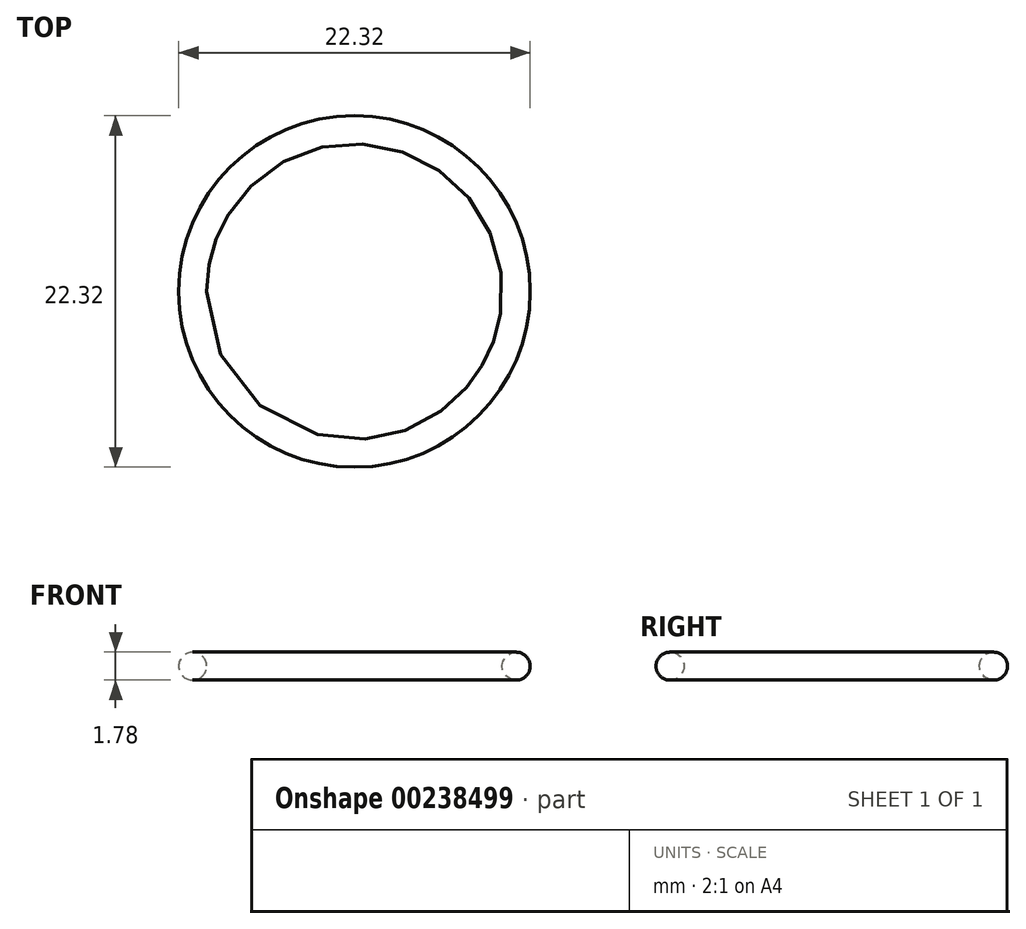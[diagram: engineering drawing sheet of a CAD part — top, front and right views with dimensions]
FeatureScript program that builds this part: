
annotation { "Feature Type Name" : "Feature", "Feature Type Description" : "" }
export const myFeature = defineFeature(function(context is Context, id is Id, definition is map)
    precondition{}
    {
        {
            var Q0;
            Q0=qCreatedBy(makeId("Front.planeOp"),FACE);
            var sketch = newSketch(context, id + "F0", { "sketchPlane" : qUnion([Q0])});
            skCircle(sketch, "E0", {"center": v(-10.27, 0) * mm, "radius": 0.89 * mm});
            skLineSegment(sketch, "E1", {"start": v(0, 0) * mm, "end": v(0, 8.6) * mm, "construction": true});
            skSolve(sketch);
        }
        {
            var Q0;
            Q0 = qSketchRegion(id + "F0", true);
            var Q1;
            Q1=sQuery(id+"F0.wireOp",EDGE,"E1");
            revolve(context, id + "F1", {"entities" : qUnion([Q0]), "axis" : qUnion([Q1]), "revolveType" : RevolveType.FULL});
        }
    });
